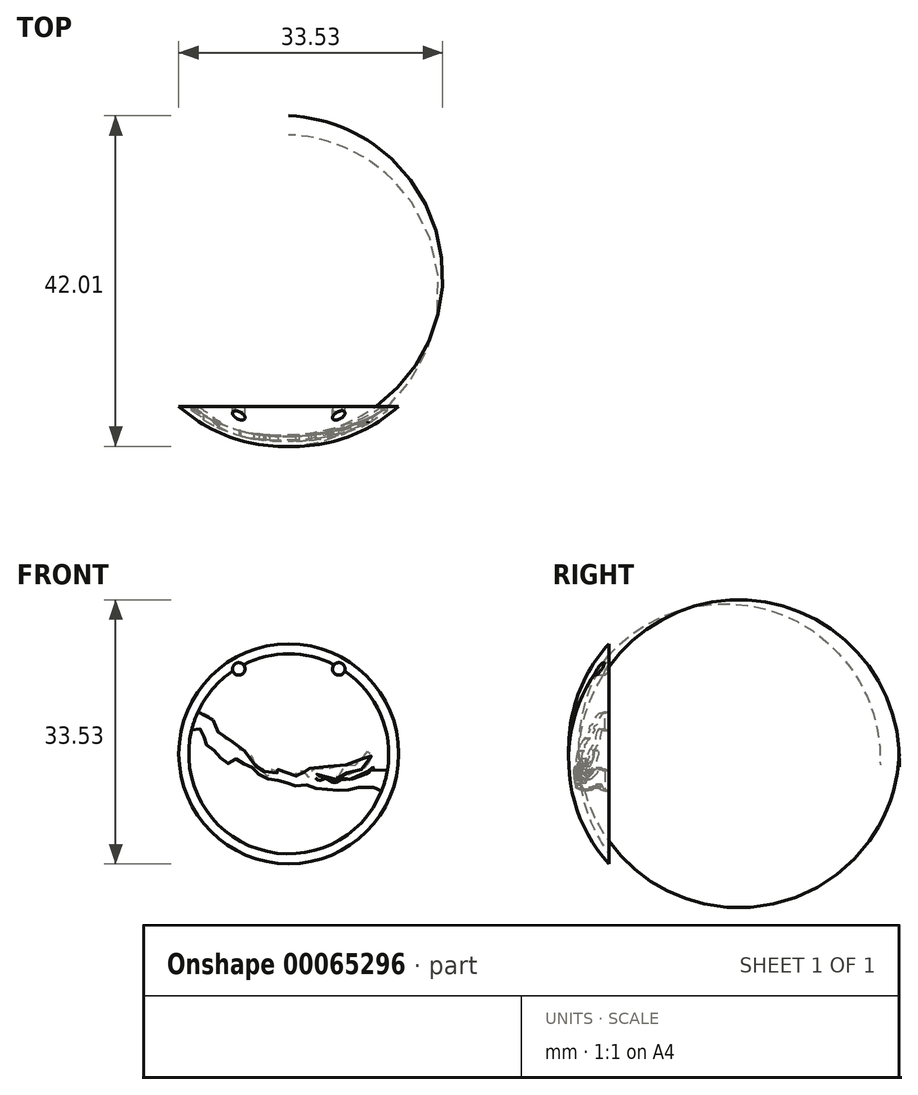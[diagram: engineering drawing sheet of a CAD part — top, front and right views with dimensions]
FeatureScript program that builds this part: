
annotation { "Feature Type Name" : "Feature", "Feature Type Description" : "" }
export const myFeature = defineFeature(function(context is Context, id is Id, definition is map)
    precondition{}
    {
        {
            var Q0;
            Q0=qCreatedBy(makeId("Front.planeOp"),FACE);
            var sketch = newSketch(context, id + "F0", { "sketchPlane" : qUnion([Q0])});
            skLineSegment(sketch, "E0", {"start": v(0, 12.7) * mm, "end": v(0, -12.7) * mm, "construction": true});
            skLineSegment(sketch, "E1", {"start": v(-12.7, 0) * mm, "end": v(12.7, 0) * mm, "construction": true});
            skPoint(sketch, "E2", {"position": v(0, 0) * mm});
            skFitSpline(sketch, "E3", {"points": [v(-11.53, 5.33) * mm, v(-10.76, 5.14) * mm, v(-10.21, 4.96) * mm, v(-9.9, 4.58) * mm, v(-9.72, 4.4) * mm, v(-9.45, 4.07) * mm, v(-9.54, 3.76) * mm, v(-9.4, 3.62) * mm, v(-8.83, 3.47) * mm, v(-8.81, 3.25) * mm, v(-9.14, 3.1) * mm, v(-9.1, 2.88) * mm, v(-8.76, 2.63) * mm, v(-8.49, 2.13) * mm, v(-8.26, 1.96) * mm, v(-7.96, 2.01) * mm, v(-7.67, 1.75) * mm, v(-7.32, 1.67) * mm, v(-7.02, 1.43) * mm, v(-6.8, 1.26) * mm, v(-6.21, 1.14) * mm, v(-6.08, 0.9) * mm, v(-6.26, 0.5) * mm, v(-6.2, 0.35) * mm, v(-5.81, 0.41) * mm, v(-5.17, 0.16) * mm, v(-4.37, -0.72) * mm, v(-4.35, -0.86) * mm, v(-4.36, -1.35) * mm, v(-4.12, -1.61) * mm, v(-3.82, -1.68) * mm, v(-3.38, -1.58) * mm, v(-3.13, -1.83) * mm, v(-3.67, -2.03) * mm, v(-3.69, -2.18) * mm, v(-3.43, -2.2) * mm, v(-2.87, -2.38) * mm, v(-2.91, -2.65) * mm, v(-2.75, -2.82) * mm, v(-2.27, -2.82) * mm, v(-2.06, -2.38) * mm, v(-1.8, -2.2) * mm, v(-1.44, -2.42) * mm, v(-1.28, -2.34) * mm, v(-1.75, -2.06) * mm, v(-2.24, -1.94) * mm, v(-2.4, -1.77) * mm, v(-1.87, -1.76) * mm, v(-1.46, -1.98) * mm, v(-0.73, -2.28) * mm, v(-0.57, -2.45) * mm, v(-0.39, -2.4) * mm, v(0.6, -2.73) * mm, v(1.27, -2.81) * mm, v(1.34, -2.59) * mm, v(0.96, -2.38) * mm, v(1.04, -2) * mm, v(1.37, -2) * mm, v(2.06, -2.34) * mm, v(2.46, -2.92) * mm, v(2.9, -2.95) * mm, v(2.62, -2.09) * mm, v(2.67, -1.82) * mm, v(3.16, -1.94) * mm, v(3.81, -1.76) * mm, v(4.5, -1.82) * mm, v(4.93, -1.59) * mm, v(5.38, -1.84) * mm, v(5.74, -1.64) * mm, v(6.05, -1.53) * mm, v(6.52, -1.55) * mm, v(6.76, -1.57) * mm, v(7.13, -1.41) * mm, v(7.96, -1.63) * mm, v(8.58, -1.32) * mm, v(9.35, -0.59) * mm, v(9.97, 0.28) * mm, v(10.34, 0.47) * mm, v(10.63, 0.13) * mm, v(10.54, -0.2) * mm, v(10.07, -1.11) * mm, v(10.04, -1.73) * mm, v(9.67, -2) * mm, v(9.08, -2.03) * mm, v(8.55, -2.35) * mm, v(8.05, -2.23) * mm, v(7.88, -2.64) * mm, v(7.7, -2.77) * mm, v(7.4, -2.4) * mm, v(7.12, -1.98) * mm, v(6.54, -2.05) * mm, v(6.37, -2.32) * mm, v(6.4, -2.61) * mm, v(5.96, -3.23) * mm, v(5.42, -3.14) * mm, v(4.48, -3.03) * mm, v(4.08, -3) * mm, v(3.81, -2.68) * mm, v(3.59, -2.6) * mm, v(3.42, -3.03) * mm, v(3.7, -3.35) * mm, v(4.16, -3.36) * mm, v(4.7, -3.14) * mm, v(5.4, -3.5) * mm, v(5.9, -3.67) * mm, v(6.37, -3.39) * mm, v(7.18, -3.15) * mm, v(7.8, -3.22) * mm, v(9.4, -2.73) * mm, v(10.2, -2.32) * mm, v(10.42, -1.91) * mm, v(11.03, -1.73) * mm, v(11.46, -1.95) * mm, v(11.88, -1.9) * mm, v(12.1, -2.06) * mm, v(12.53, -2.06) * mm, v(12.34, -1.72) * mm, v(12.46, -1.52) * mm, v(12.61, -1.49) * mm], "startDerivative": vector(71.47, -19.35) * mm, "endDerivative": vector(20.75, 2.08) * mm});
            skFitSpline(sketch, "E4", {"points": [v(-12.33, 3.03) * mm, v(-12.06, 2.98) * mm, v(-11.5, 3.13) * mm, v(-11.15, 3.11) * mm, v(-10.81, 2.45) * mm, v(-10.8, 1.57) * mm, v(-10.74, 1.24) * mm, v(-10.2, 1.03) * mm, v(-9.81, 0.68) * mm, v(-9.36, 0.3) * mm, v(-8.99, -0.24) * mm, v(-8.39, -0.76) * mm, v(-7.98, -1.26) * mm, v(-7.62, -1.15) * mm, v(-7.09, -0.64) * mm, v(-6.72, -0.64) * mm, v(-6.28, -1.15) * mm, v(-5.52, -1.27) * mm, v(-4.94, -1.3) * mm, v(-4.56, -2.03) * mm, v(-4.08, -2.53) * mm, v(-3.33, -2.82) * mm, v(-2.93, -3.15) * mm, v(-2.36, -3.18) * mm, v(-1.8, -3.2) * mm, v(-1.44, -3.4) * mm, v(-1.23, -3.27) * mm, v(-0.73, -3.31) * mm, v(-0.38, -3.73) * mm, v(-0.18, -3.7) * mm, v(0.2, -4.15) * mm, v(0.61, -4.28) * mm, v(0.85, -4.1) * mm, v(2, -3.94) * mm, v(2.56, -4.1) * mm, v(2.92, -4.42) * mm, v(3.26, -4.32) * mm, v(3.6, -4.4) * mm, v(4.54, -4.5) * mm, v(5.85, -4.63) * mm, v(6.24, -4.64) * mm, v(6.49, -4.45) * mm, v(7.11, -4.59) * mm, v(7.89, -4.51) * mm, v(8.36, -4.4) * mm, v(8.58, -4.23) * mm, v(8.94, -4.28) * mm, v(9.38, -4.27) * mm, v(9.64, -4.06) * mm, v(9.78, -4.1) * mm, v(9.96, -4.26) * mm, v(10.24, -4.3) * mm, v(10.37, -4) * mm, v(10.5, -3.83) * mm, v(10.66, -4.1) * mm, v(10.89, -4.43) * mm, v(11.8, -4.68) * mm], "startDerivative": vector(18.26, -5.68) * mm, "endDerivative": vector(44.35, -7.18) * mm});
            skFitSpline(sketch, "E5", {"points": [v(-10.45, 7.22) * mm, v(-8.56, 6.35) * mm, v(-7.58, 5.18) * mm, v(-6.18, 3.75) * mm, v(-5.45, 2.93) * mm, v(-3.1, 2.07) * mm, v(-2.7, 0.49) * mm, v(-2.12, 0) * mm, v(-1.08, -0.37) * mm, v(0.6, 0) * mm, v(2.25, 0.4) * mm, v(4.89, 0.7) * mm, v(6.85, 0.93) * mm, v(8.6, 1.6) * mm, v(10.18, 2.17) * mm, v(11.83, 2) * mm, v(12.52, 2.1) * mm], "startDerivative": vector(30.17, -10.3) * mm, "endDerivative": vector(14.73, 3.98) * mm});
            skFitSpline(sketch, "E6", {"points": [v(-12.67, 0.83) * mm, v(-11.39, -0.7) * mm, v(-9.86, -2.28) * mm, v(-8.91, -3.67) * mm, v(-7.58, -4.09) * mm, v(-6.15, -3.64) * mm, v(-3.36, -5.3) * mm, v(-1.01, -5.8) * mm, v(0.8, -6.47) * mm, v(2.76, -6.08) * mm, v(6.38, -6.56) * mm, v(7.9, -6.18) * mm, v(9.68, -6.02) * mm, v(10.97, -6.4) * mm], "startDerivative": vector(15.55, -20.1) * mm, "endDerivative": vector(19.16, -7.52) * mm});
            skArc(sketch, "E7", {"start": v(12.52, 2.1) * mm, "mid": v(2.76, 12.4) * mm, "end": v(-10.45, 7.22) * mm});
            skArc(sketch, "E8", {"start": v(10.97, -6.4) * mm, "mid": v(12.5, -2.28) * mm, "end": v(12.52, 2.1) * mm});
            skArc(sketch, "E9", {"start": v(-10.45, 7.22) * mm, "mid": v(-12, 4.17) * mm, "end": v(-12.67, 0.83) * mm});
            skArc(sketch, "E10", {"start": v(-12.67, 0.83) * mm, "mid": v(-3.71, -12.15) * mm, "end": v(10.97, -6.4) * mm});
            skSolve(sketch);
        }
        {
            var Q0;
            Q0=qCreatedBy(makeId("Right.planeOp"),FACE);
            var sketch = newSketch(context, id + "F1", { "sketchPlane" : qUnion([Q0])});
            skArc(sketch, "E11", {"start": v(0, 13.97) * mm, "mid": v(-3.9, 7.48) * mm, "end": v(-5.08, 0) * mm});
            skArc(sketch, "E12", {"start": v(0, 12.7) * mm, "mid": v(-2.97, 6.67) * mm, "end": v(-3.81, 0) * mm});
            skLineSegment(sketch, "E13", {"start": v(-5.08, 0) * mm, "end": v(-3.81, 0) * mm});
            skLineSegment(sketch, "E14", {"start": v(0, 12.7) * mm, "end": v(0, 13.97) * mm});
            skLineSegment(sketch, "E15", {"start": v(-3.81, 0) * mm, "end": v(0, 0) * mm, "construction": true});
            skArc(sketch, "E16", {"start": v(0, 13.33) * mm, "mid": v(-3.46, 7.08) * mm, "end": v(-4.44, 0) * mm});
            skSolve(sketch);
        }
        {
            var Q0;
            Q0 = qSketchRegion(id + "F1", true);
            var Q1;
            Q1=sQuery(id+"F1.wireOp",EDGE,"E15");
            revolve(context, id + "F2", {"entities" : qUnion([Q0]), "axis" : qUnion([Q1]), "revolveType" : RevolveType.FULL});
        }
        {
            var Q0;
            {var subQ0=sQuery(id+"F1.wireOp",EDGE,"E12");Q0=makeQuery(id+"F1.imprint","IMPRINT",FACE,{"disambiguationData":[TD([[makeQuery(id+"F1.imprint","IMPRINT",EDGE,{"derivedFrom":subQ0}),-1.0]])]});}
            var Q1;
            Q1=sQuery(id+"F1.wireOp",EDGE,"E15");
            revolve(context, id + "F3", {"entities" : qUnion([Q0]), "axis" : qUnion([Q1]), "revolveType" : RevolveType.FULL});
        }
        {
            var Q0;
            {var subQ3=sQuery(id+"F0.wireOp",EDGE,"E4");Q0=makeQuery(id+"F0.imprint","IMPRINT",FACE,{"disambiguationData":[TD([[makeQuery(id+"F0.imprint","IMPRINT",EDGE,{"derivedFrom":subQ3}),1.0]])]});}
            extrude(context, id + "F4", {"entities" : qUnion([Q0]), "depth" : 25.4 * mm});
        }
        {
            var Q0;
            Q0=makeQuery(id+"F3.opRevolve","SWEPT_BODY",BODY,{"disambiguationData":[OSD([sQuery(id+"F1.wireOp",EDGE,"E12"),sQuery(id+"F1.wireOp",EDGE,"E13"),sQuery(id+"F1.wireOp",EDGE,"E14"),sQuery(id+"F1.wireOp",EDGE,"E16")])]});
            var Q1;
            Q1=makeQuery(id+"F4.opExtrude","SWEPT_BODY",BODY,{"disambiguationData":[OSD([sQuery(id+"F0.wireOp",EDGE,"55987371-a79b-4012-9764-dc91cd294edf"),sQuery(id+"F0.wireOp",EDGE,"E3"),sQuery(id+"F0.wireOp",EDGE,"E4")])]});
            booleanBodies(context, id + "F5", {"operationType" : BooleanOperationType.INTERSECTION, "tools" : qUnion([Q0, Q1])});
        }
        {
            var Q0;
            Q0=makeQuery(id+"F5.opBoolean","INTERSECT",BODY,{"derivedFrom":[makeQuery(id+"F3.opRevolve","SWEPT_BODY",BODY,{"disambiguationData":[OSD([sQuery(id+"F1.wireOp",EDGE,"E12"),sQuery(id+"F1.wireOp",EDGE,"E13"),sQuery(id+"F1.wireOp",EDGE,"E14"),sQuery(id+"F1.wireOp",EDGE,"E16")])]}),makeQuery(id+"F4.opExtrude","SWEPT_BODY",BODY,{"disambiguationData":[OSD([sQuery(id+"F0.wireOp",EDGE,"55987371-a79b-4012-9764-dc91cd294edf"),sQuery(id+"F0.wireOp",EDGE,"E3"),sQuery(id+"F0.wireOp",EDGE,"E4")])]})]});
            var Q1;
            Q1=makeQuery(id+"F2.opRevolve","SWEPT_BODY",BODY,{"disambiguationData":[OSD([sQuery(id+"F1.wireOp",EDGE,"E11"),sQuery(id+"F1.wireOp",EDGE,"E12"),sQuery(id+"F1.wireOp",EDGE,"E13"),sQuery(id+"F1.wireOp",EDGE,"E14")])]});
            booleanBodies(context, id + "F6", {"operationType" : BooleanOperationType.SUBTRACTION, "tools" : qUnion([Q0]), "targets" : qUnion([Q1])});
        }
        {
            var Q0;
            Q0=qCreatedBy(makeId("Front.planeOp"),FACE);
            var sketch = newSketch(context, id + "F7", { "sketchPlane" : qUnion([Q0])});
            skCircle(sketch, "E17", {"center": v(-6.35, 10.8) * mm, "radius": 0.8 * mm});
            skCircle(sketch, "E18", {"center": v(6.35, 10.8) * mm, "radius": 0.8 * mm});
            skLineSegment(sketch, "E19", {"start": v(-6.35, 10.8) * mm, "end": v(6.35, 10.8) * mm, "construction": true});
            skPoint(sketch, "E20", {"position": v(0, 10.8) * mm});
            skSolve(sketch);
        }
        {
            var Q0;
            Q0 = qSketchRegion(id + "F7", true);
            extrude(context, id + "F8", {"entities" : qUnion([Q0]), "operationType" : NewBodyOperationType.REMOVE, "depth" : 25.4 * mm});
        }
    });
